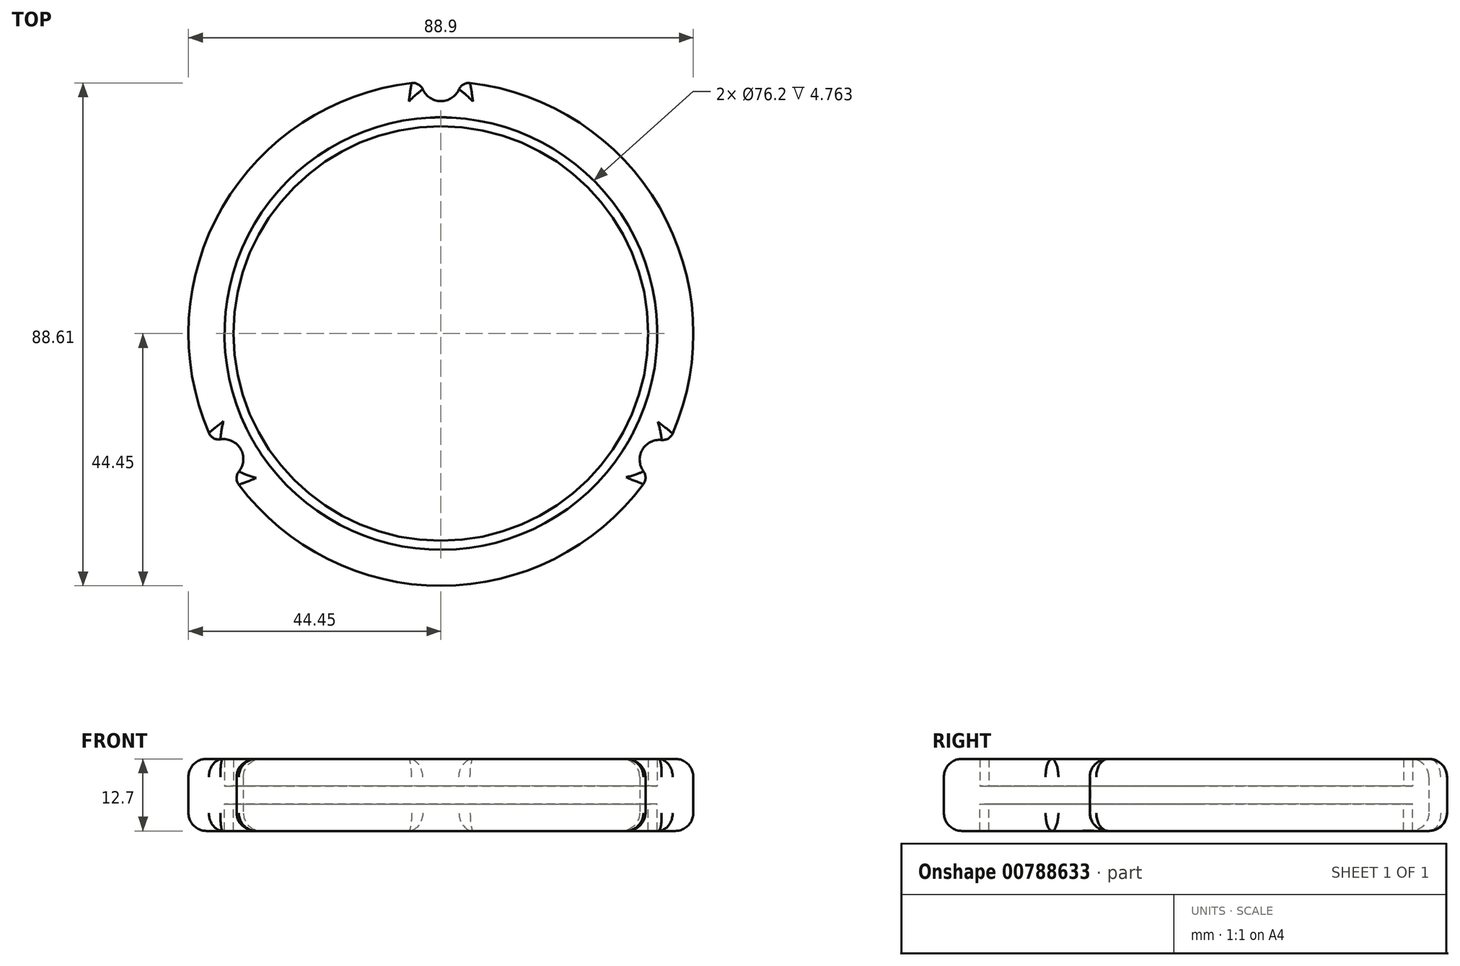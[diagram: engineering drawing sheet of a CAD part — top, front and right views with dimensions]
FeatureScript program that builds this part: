
annotation { "Feature Type Name" : "Feature", "Feature Type Description" : "" }
export const myFeature = defineFeature(function(context is Context, id is Id, definition is map)
    precondition{}
    {
        {
            var Q0;
            Q0=qCreatedBy(makeId("Top.planeOp"),FACE);
            var sketch = newSketch(context, id + "F0", { "sketchPlane" : qUnion([Q0])});
            skCircle(sketch, "E0", {"center": v(0, 0) * mm, "radius": 38.1 * mm});
            skCircle(sketch, "E1", {"center": v(0, 0) * mm, "radius": 36.51 * mm});
            skArc(sketch, "E2", {"start": v(-5.15, 44.15) * mm, "mid": v(-38.47, 22.27) * mm, "end": v(-40.85, -17.52) * mm});
            skLineSegment(sketch, "E3", {"start": v(0, 0) * mm, "end": v(0, 53.56) * mm});
            skLineSegment(sketch, "E4", {"start": v(0, 53.56) * mm, "end": v(0, 44.45) * mm});
            skLineSegment(sketch, "E5", {"start": v(55.5, -32.04) * mm, "end": v(0, 0) * mm});
            skLineSegment(sketch, "E6", {"start": v(-47.97, -27.7) * mm, "end": v(0, 0) * mm});
            skArc(sketch, "E7", {"start": v(-35.56, -24.29) * mm, "mid": v(-35.25, -20.35) * mm, "end": v(-38.81, -18.65) * mm});
            skArc(sketch, "E8", {"start": v(38.86, -18.75) * mm, "mid": v(35.47, -20.48) * mm, "end": v(35.67, -24.28) * mm});
            skArc(sketch, "E9", {"start": v(-3.2, 43.03) * mm, "mid": v(0, 40.96) * mm, "end": v(3.2, 43.03) * mm});
            skLineSegment(sketch, "E10.trimOffspring", {"start": v(0, 40.96) * mm, "end": v(0, 0) * mm});
            skArc(sketch, "E11.trimOffspring", {"start": v(-35.6, -26.62) * mm, "mid": v(0.05, -44.45) * mm, "end": v(35.66, -26.54) * mm});
            skArc(sketch, "E12.trimOffspring", {"start": v(40.81, -17.61) * mm, "mid": v(38.5, 22.23) * mm, "end": v(5.15, 44.15) * mm});
            skPoint(sketch, "E13.visualSharp", {"position": v(40.12, -19.13) * mm});
            skArc(sketch, "E13.filletArc", {"start": v(38.86, -18.75) * mm, "mid": v(40.02, -18.5) * mm, "end": v(40.81, -17.61) * mm});
            skPoint(sketch, "E14.visualSharp", {"position": v(36.63, -25.18) * mm});
            skArc(sketch, "E14.filletArc", {"start": v(35.66, -26.54) * mm, "mid": v(36.04, -25.41) * mm, "end": v(35.67, -24.28) * mm});
            skPoint(sketch, "E15.visualSharp", {"position": v(-36.63, -25.18) * mm});
            skArc(sketch, "E15.filletArc", {"start": v(-35.56, -24.29) * mm, "mid": v(-35.98, -25.45) * mm, "end": v(-35.6, -26.62) * mm});
            skPoint(sketch, "E16.visualSharp", {"position": v(-40.12, -19.13) * mm});
            skArc(sketch, "E16.filletArc", {"start": v(-40.85, -17.52) * mm, "mid": v(-40.03, -18.43) * mm, "end": v(-38.81, -18.65) * mm});
            skPoint(sketch, "E17.visualSharp", {"position": v(-3.49, 44.31) * mm});
            skArc(sketch, "E17.filletArc", {"start": v(-3.2, 43.03) * mm, "mid": v(-3.99, 43.91) * mm, "end": v(-5.15, 44.15) * mm});
            skPoint(sketch, "E18.visualSharp", {"position": v(3.49, 44.31) * mm});
            skArc(sketch, "E18.filletArc", {"start": v(5.15, 44.15) * mm, "mid": v(3.99, 43.91) * mm, "end": v(3.2, 43.03) * mm});
            skSolve(sketch);
        }
        {
            var Q0;
            Q0=makeQuery(id+"F0.imprint","IMPRINT",FACE,{"disambiguationData":[TD([[makeQuery(id+"F0.imprint","IMPRINT",EDGE,{"derivedFrom":sQuery(id+"F0.wireOp",EDGE,"E2")}),1.0]])]});
            var Q1;
            Q1=makeQuery(id+"F0.imprint","IMPRINT",FACE,{"disambiguationData":[TD([[makeQuery(id+"F0.imprint","IMPRINT",EDGE,{"derivedFrom":sQuery(id+"F0.wireOp",EDGE,"E12.trimOffspring")}),1.0]])]});
            var Q2;
            {var subQ0=sQuery(id+"F0.wireOp",EDGE,"E10.trimOffspring");var subQ1=sQuery(id+"F0.wireOp",EDGE,"E1");var subQ2=makeQuery(id+"F0.imprint","INTERSECT",VERTEX,{"derivedFrom":[subQ1,subQ0]});Q2=makeQuery(id+"F0.imprint","IMPRINT",FACE,{"disambiguationData":[TD([[makeQuery(id+"F0.imprint","IMPRINT",EDGE,{"disambiguationData":[TD([[subQ2,1.0]])],"derivedFrom":subQ1}),1.0]])]});}
            var Q3;
            {var subQ0=sQuery(id+"F0.wireOp",EDGE,"E6");var subQ1=sQuery(id+"F0.wireOp",EDGE,"E1");var subQ2=makeQuery(id+"F0.imprint","INTERSECT",VERTEX,{"derivedFrom":[subQ1,subQ0]});Q3=makeQuery(id+"F0.imprint","IMPRINT",FACE,{"disambiguationData":[TD([[makeQuery(id+"F0.imprint","IMPRINT",EDGE,{"disambiguationData":[TD([[subQ2,1.0]])],"derivedFrom":subQ1}),1.0]])]});}
            var Q4;
            Q4=makeQuery(id+"F0.imprint","IMPRINT",FACE,{"disambiguationData":[TD([[makeQuery(id+"F0.imprint","IMPRINT",EDGE,{"derivedFrom":sQuery(id+"F0.wireOp",EDGE,"E11.trimOffspring")}),1.0]])]});
            var Q5;
            {var subQ0=sQuery(id+"F0.wireOp",EDGE,"E6");var subQ1=sQuery(id+"F0.wireOp",EDGE,"E1");var subQ2=makeQuery(id+"F0.imprint","INTERSECT",VERTEX,{"derivedFrom":[subQ1,subQ0]});Q5=makeQuery(id+"F0.imprint","IMPRINT",FACE,{"disambiguationData":[TD([[makeQuery(id+"F0.imprint","IMPRINT",EDGE,{"disambiguationData":[TD([[subQ2,-1.0]])],"derivedFrom":subQ1}),1.0]])]});}
            extrude(context, id + "F1", {"entities" : qUnion([Q0, Q1, Q2, Q3, Q4, Q5]), "depth" : 4.76 * mm, "offsetDistance" : 25.4 * mm});
        }
        {
            var Q0;
            Q0=makeQuery(id+"F1.opExtrude","CAP_FACE",FACE,{"disambiguationData":[OSD([sQuery(id+"F0.wireOp",EDGE,"E1")])],"isStart":true});
            var sketch = newSketch(context, id + "F2", { "sketchPlane" : qUnion([Q0])});
            skArc(sketch, "E19.0", {"start": v(-35.6, 26.62) * mm, "mid": v(0.05, 44.45) * mm, "end": v(35.66, 26.54) * mm});
            skArc(sketch, "E20.0.0", {"start": v(35.67, 24.28) * mm, "mid": v(36.04, 25.41) * mm, "end": v(35.66, 26.54) * mm});
            skArc(sketch, "E20.0.1", {"start": v(35.66, 26.54) * mm, "mid": v(0.05, 44.45) * mm, "end": v(-35.6, 26.62) * mm});
            skArc(sketch, "E20.0.2", {"start": v(-35.6, 26.62) * mm, "mid": v(-35.98, 25.45) * mm, "end": v(-35.56, 24.29) * mm});
            skArc(sketch, "E20.0.3", {"start": v(-35.56, 24.29) * mm, "mid": v(-35.25, 20.35) * mm, "end": v(-38.81, 18.65) * mm});
            skArc(sketch, "E20.0.4", {"start": v(-38.81, 18.65) * mm, "mid": v(-40.03, 18.43) * mm, "end": v(-40.85, 17.52) * mm});
            skArc(sketch, "E20.0.5", {"start": v(-40.85, 17.52) * mm, "mid": v(-38.47, -22.27) * mm, "end": v(-5.15, -44.15) * mm});
            skArc(sketch, "E20.0.6", {"start": v(-5.15, -44.15) * mm, "mid": v(-3.99, -43.91) * mm, "end": v(-3.2, -43.03) * mm});
            skArc(sketch, "E20.0.7", {"start": v(-3.2, -43.03) * mm, "mid": v(0, -40.96) * mm, "end": v(3.2, -43.03) * mm});
            skArc(sketch, "E20.0.8", {"start": v(3.2, -43.03) * mm, "mid": v(3.99, -43.91) * mm, "end": v(5.15, -44.15) * mm});
            skArc(sketch, "E20.0.9", {"start": v(5.15, -44.15) * mm, "mid": v(38.5, -22.23) * mm, "end": v(40.81, 17.61) * mm});
            skArc(sketch, "E20.0.10", {"start": v(40.81, 17.61) * mm, "mid": v(40.02, 18.5) * mm, "end": v(38.86, 18.75) * mm});
            skArc(sketch, "E20.0.11", {"start": v(38.86, 18.75) * mm, "mid": v(35.47, 20.48) * mm, "end": v(35.67, 24.28) * mm});
            skCircle(sketch, "E21.0.0", {"center": v(0, 0) * mm, "radius": 36.51 * mm});
            skCircle(sketch, "E22.0", {"center": v(0, 0) * mm, "radius": 38.1 * mm});
            skSolve(sketch);
        }
        {
            var Q0;
            Q0=makeQuery(id+"F2.imprint","IMPRINT",FACE,{"disambiguationData":[TD([[makeQuery(id+"F2.imprint","IMPRINT",EDGE,{"derivedFrom":sQuery(id+"F2.wireOp",EDGE,"E20.0.0")}),1.0]])]});
            var Q1;
            Q1=makeQuery(id+"F2.imprint","IMPRINT",FACE,{"disambiguationData":[TD([[makeQuery(id+"F2.imprint","IMPRINT",EDGE,{"derivedFrom":sQuery(id+"F2.wireOp",EDGE,"E21.0.0")}),-1.0]])]});
            var Q2;
            Q2=makeQuery(id+"F2.imprint","IMPRINT",FACE,{"disambiguationData":[TD([[makeQuery(id+"F2.imprint","IMPRINT",EDGE,{"derivedFrom":sQuery(id+"F2.wireOp",EDGE,"E21.0.0")}),1.0]])]});
            extrude(context, id + "F3", {"entities" : qUnion([Q0, Q1, Q2]), "operationType" : NewBodyOperationType.ADD, "depth" : 3.17 * mm, "offsetDistance" : 25.4 * mm});
        }
        {
            var Q0;
            Q0=makeQuery(id+"F3.opExtrude","CAP_FACE",FACE,{"disambiguationData":[OSD([sQuery(id+"F2.wireOp",EDGE,"E20.0.0"),sQuery(id+"F2.wireOp",EDGE,"E20.0.1"),sQuery(id+"F2.wireOp",EDGE,"E20.0.2"),sQuery(id+"F2.wireOp",EDGE,"E20.0.3"),sQuery(id+"F2.wireOp",EDGE,"E20.0.4"),sQuery(id+"F2.wireOp",EDGE,"E20.0.5"),sQuery(id+"F2.wireOp",EDGE,"E20.0.6"),sQuery(id+"F2.wireOp",EDGE,"E20.0.7"),sQuery(id+"F2.wireOp",EDGE,"E20.0.8"),sQuery(id+"F2.wireOp",EDGE,"E20.0.9"),sQuery(id+"F2.wireOp",EDGE,"E20.0.10"),sQuery(id+"F2.wireOp",EDGE,"E20.0.11")])],"isStart":false});
            var sketch = newSketch(context, id + "F4", { "sketchPlane" : qUnion([Q0])});
            skCircle(sketch, "E23.0.0", {"center": v(0, 0) * mm, "radius": 36.51 * mm});
            skCircle(sketch, "E24.0", {"center": v(0, 0) * mm, "radius": 38.1 * mm});
            skArc(sketch, "E25.0.0", {"start": v(35.66, 26.54) * mm, "mid": v(36.04, 25.41) * mm, "end": v(35.67, 24.28) * mm});
            skArc(sketch, "E25.0.1", {"start": v(35.67, 24.28) * mm, "mid": v(35.47, 20.48) * mm, "end": v(38.86, 18.75) * mm});
            skArc(sketch, "E25.0.2", {"start": v(38.86, 18.75) * mm, "mid": v(40.02, 18.5) * mm, "end": v(40.81, 17.61) * mm});
            skArc(sketch, "E25.0.3", {"start": v(40.81, 17.61) * mm, "mid": v(38.5, -22.23) * mm, "end": v(5.15, -44.15) * mm});
            skArc(sketch, "E25.0.4", {"start": v(5.15, -44.15) * mm, "mid": v(3.99, -43.91) * mm, "end": v(3.2, -43.03) * mm});
            skArc(sketch, "E25.0.5", {"start": v(3.2, -43.03) * mm, "mid": v(0, -40.96) * mm, "end": v(-3.2, -43.03) * mm});
            skArc(sketch, "E25.0.6", {"start": v(-3.2, -43.03) * mm, "mid": v(-3.99, -43.91) * mm, "end": v(-5.15, -44.15) * mm});
            skArc(sketch, "E25.0.7", {"start": v(-5.15, -44.15) * mm, "mid": v(-38.47, -22.27) * mm, "end": v(-40.85, 17.52) * mm});
            skArc(sketch, "E25.0.8", {"start": v(-40.85, 17.52) * mm, "mid": v(-40.03, 18.43) * mm, "end": v(-38.81, 18.65) * mm});
            skArc(sketch, "E25.0.9", {"start": v(-38.81, 18.65) * mm, "mid": v(-35.25, 20.35) * mm, "end": v(-35.56, 24.29) * mm});
            skArc(sketch, "E25.0.10", {"start": v(-35.56, 24.29) * mm, "mid": v(-35.98, 25.45) * mm, "end": v(-35.6, 26.62) * mm});
            skArc(sketch, "E25.0.11", {"start": v(-35.6, 26.62) * mm, "mid": v(0.05, 44.45) * mm, "end": v(35.66, 26.54) * mm});
            skSolve(sketch);
        }
        {
            var Q0;
            Q0=makeQuery(id+"F4.imprint","IMPRINT",FACE,{"disambiguationData":[TD([[makeQuery(id+"F4.imprint","IMPRINT",EDGE,{"derivedFrom":sQuery(id+"F4.wireOp",EDGE,"E24.0")}),-1.0]])]});
            var Q1;
            Q1=makeQuery(id+"F4.imprint","IMPRINT",FACE,{"disambiguationData":[TD([[makeQuery(id+"F4.imprint","IMPRINT",EDGE,{"derivedFrom":sQuery(id+"F4.wireOp",EDGE,"E23.0.0")}),1.0]])]});
            extrude(context, id + "F5", {"entities" : qUnion([Q0, Q1]), "operationType" : NewBodyOperationType.ADD, "depth" : 4.76 * mm, "offsetDistance" : 25.4 * mm});
        }
        {
            var Q0;
            Q0=makeQuery(id+"F1.opExtrude","CAP_EDGE",EDGE,{"disambiguationData":[OSD([sQuery(id+"F0.wireOp",EDGE,"E11.trimOffspring")])],"isStart":false});
            var Q1;
            Q1=makeQuery(id+"F1.opExtrude","CAP_EDGE",EDGE,{"disambiguationData":[OSD([sQuery(id+"F0.wireOp",EDGE,"E12.trimOffspring")])],"isStart":false});
            var Q2;
            Q2=makeQuery(id+"F5.opExtrude","CAP_EDGE",EDGE,{"disambiguationData":[OSD([sQuery(id+"F4.wireOp",EDGE,"E25.0.3")])],"isStart":false});
            fillet(context, id + "F6", {"entities" : qUnion([Q0, Q1, Q2]), "radius" : 3.17 * mm, "tangentPropagation" : true, "allowEdgeOverflow" : false});
        }
    });
